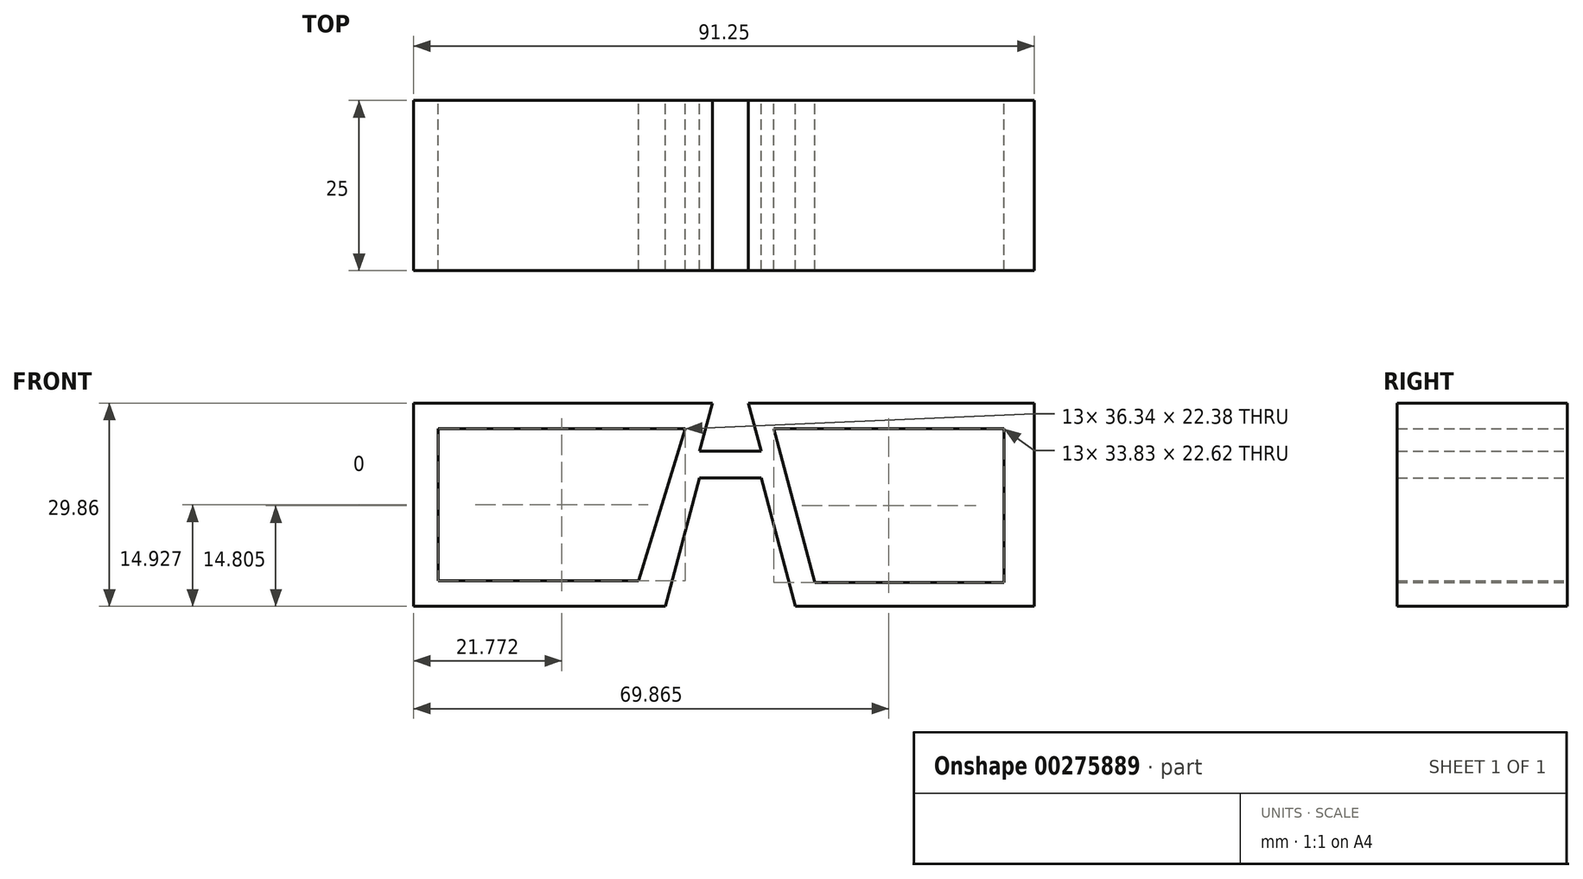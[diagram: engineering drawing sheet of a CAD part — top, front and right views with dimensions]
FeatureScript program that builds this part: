
annotation { "Feature Type Name" : "Feature", "Feature Type Description" : "" }
export const myFeature = defineFeature(function(context is Context, id is Id, definition is map)
    precondition{}
    {
        {
            var Q0;
            Q0=qCreatedBy(makeId("Front.planeOp"),FACE);
            var sketch = newSketch(context, id + "F0", { "sketchPlane" : qUnion([Q0])});
            skLineSegment(sketch, "E0", {"start": v(43.93, 0) * mm, "end": v(42.04, -7.03) * mm});
            skLineSegment(sketch, "E1", {"start": v(42.04, -7.03) * mm, "end": v(51.1, -7.03) * mm});
            skLineSegment(sketch, "E2", {"start": v(51.1, -7.03) * mm, "end": v(49.2, 0) * mm});
            skLineSegment(sketch, "E3", {"start": v(49.2, 0) * mm, "end": v(91.25, 0) * mm});
            skLineSegment(sketch, "E4", {"start": v(91.25, 0) * mm, "end": v(91.25, -29.86) * mm});
            skLineSegment(sketch, "E5", {"start": v(91.25, -29.86) * mm, "end": v(56.14, -29.86) * mm});
            skLineSegment(sketch, "E6", {"start": v(51.1, -11) * mm, "end": v(42.04, -11) * mm});
            skLineSegment(sketch, "E7", {"start": v(37, -29.86) * mm, "end": v(0, -29.86) * mm});
            skLineSegment(sketch, "E8", {"start": v(0, -29.86) * mm, "end": v(0, 0) * mm});
            skLineSegment(sketch, "E9", {"start": v(42.04, -11) * mm, "end": v(37, -29.86) * mm});
            skLineSegment(sketch, "E10", {"start": v(51.1, -11) * mm, "end": v(56.14, -29.86) * mm});
            skLineSegment(sketch, "E11", {"start": v(0, 0) * mm, "end": v(43.93, 0) * mm});
            skLineSegment(sketch, "E12", {"start": v(3.6, -3.74) * mm, "end": v(3.6, -26.12) * mm});
            skLineSegment(sketch, "E13", {"start": v(3.6, -26.12) * mm, "end": v(33.1, -26.12) * mm});
            skLineSegment(sketch, "E14", {"start": v(33.1, -26.12) * mm, "end": v(39.94, -3.74) * mm});
            skLineSegment(sketch, "E15", {"start": v(39.94, -3.74) * mm, "end": v(3.6, -3.74) * mm});
            skLineSegment(sketch, "E16", {"start": v(86.78, -3.74) * mm, "end": v(86.78, -26.37) * mm});
            skLineSegment(sketch, "E17", {"start": v(86.78, -26.37) * mm, "end": v(59.01, -26.37) * mm});
            skLineSegment(sketch, "E18", {"start": v(59.01, -26.37) * mm, "end": v(52.95, -3.74) * mm});
            skLineSegment(sketch, "E19", {"start": v(52.95, -3.74) * mm, "end": v(86.78, -3.74) * mm});
            skSolve(sketch);
        }
        {
            var Q0;
            Q0 = qSketchRegion(id + "F0", true);
            extrude(context, id + "F1", {"entities" : qUnion([Q0]), "depth" : 25 * mm});
        }
    });
